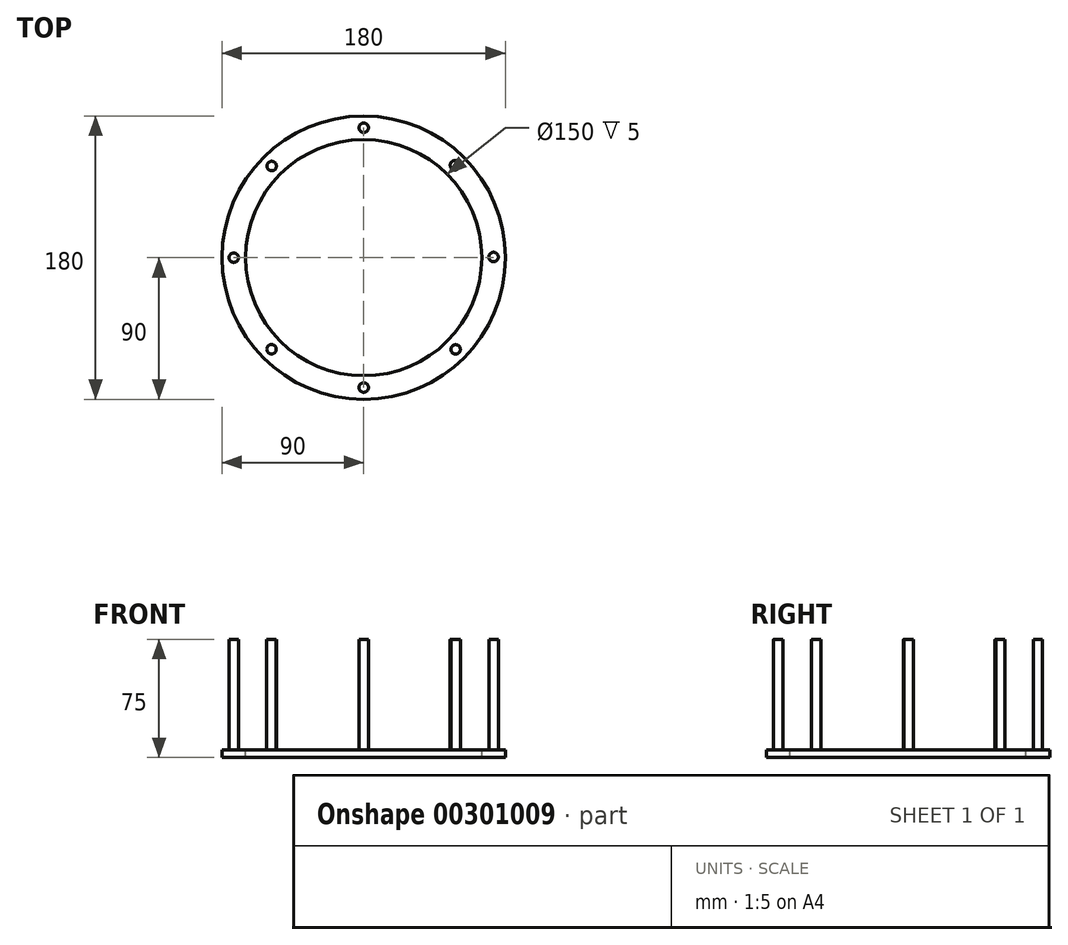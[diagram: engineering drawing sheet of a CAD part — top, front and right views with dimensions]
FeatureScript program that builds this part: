
annotation { "Feature Type Name" : "Feature", "Feature Type Description" : "" }
export const myFeature = defineFeature(function(context is Context, id is Id, definition is map)
    precondition{}
    {
        {
            var Q0;
            Q0=qCreatedBy(makeId("Top.planeOp"),FACE);
            var sketch = newSketch(context, id + "F0", { "sketchPlane" : qUnion([Q0])});
            skCircle(sketch, "E0", {"center": v(0, 0) * mm, "radius": 90 * mm});
            skCircle(sketch, "E1", {"center": v(0, 0) * mm, "radius": 75 * mm});
            skPoint(sketch, "E2", {"position": v(0, 82.48) * mm});
            skPoint(sketch, "E3", {"position": v(0, -82.5) * mm});
            skPoint(sketch, "E4", {"position": v(-75, 0) * mm});
            skPoint(sketch, "E5", {"position": v(-82.5, 0) * mm});
            skPoint(sketch, "E6", {"position": v(-58.44, 58.23) * mm});
            skPoint(sketch, "E7", {"position": v(82.5, 0.44) * mm});
            skPoint(sketch, "E8", {"position": v(57.94, 58.73) * mm});
            skPoint(sketch, "E9", {"position": v(-58.53, -58.15) * mm});
            skLineSegment(sketch, "E10", {"start": v(0, 0) * mm, "end": v(0, 0) * mm});
            skPoint(sketch, "E11", {"position": v(58.39, -58.28) * mm});
            skSolve(sketch);
        }
        {
            var Q0;
            Q0=makeQuery(id+"F0.imprint","IMPRINT",FACE,{"disambiguationData":[TD([[makeQuery(id+"F0.imprint","IMPRINT",EDGE,{"derivedFrom":sQuery(id+"F0.wireOp",EDGE,"E0")}),1.0]])]});
            extrude(context, id + "F1", {"entities" : qUnion([Q0]), "oppositeDirection" : true, "depth" : 5 * mm});
        }
        {
            var Q0;
            Q0=qCreatedBy(makeId("Top.planeOp"),FACE);
            var sketch = newSketch(context, id + "F2", { "sketchPlane" : qUnion([Q0])});
            skPoint(sketch, "E12", {"position": v(0, 82.5) * mm});
            skCircle(sketch, "E13", {"center": v(0, 82.5) * mm, "radius": 3 * mm});
            skCircle(sketch, "E14", {"center": v(57.94, 58.73) * mm, "radius": 3 * mm});
            skCircle(sketch, "E15", {"center": v(0, -82.5) * mm, "radius": 3 * mm});
            skCircle(sketch, "E16", {"center": v(-58.44, 58.22) * mm, "radius": 3 * mm});
            skCircle(sketch, "E17", {"center": v(-82.5, 0) * mm, "radius": 3 * mm});
            skCircle(sketch, "E18", {"center": v(58.4, -58.28) * mm, "radius": 3 * mm});
            skCircle(sketch, "E19", {"center": v(-58.53, -58.14) * mm, "radius": 3 * mm});
            skCircle(sketch, "E20", {"center": v(82.5, 0.44) * mm, "radius": 3 * mm});
            skSolve(sketch);
        }
        {
            var Q0;
            Q0=makeQuery(id+"F2.imprint","IMPRINT",FACE,{"disambiguationData":[TD([[makeQuery(id+"F2.imprint","IMPRINT",EDGE,{"derivedFrom":sQuery(id+"F2.wireOp",EDGE,"E13")}),1.0]])]});
            var Q1;
            Q1=makeQuery(id+"F2.imprint","IMPRINT",FACE,{"disambiguationData":[TD([[makeQuery(id+"F2.imprint","IMPRINT",EDGE,{"derivedFrom":sQuery(id+"F2.wireOp",EDGE,"E14")}),1.0]])]});
            var Q2;
            Q2=makeQuery(id+"F2.imprint","IMPRINT",FACE,{"disambiguationData":[TD([[makeQuery(id+"F2.imprint","IMPRINT",EDGE,{"derivedFrom":sQuery(id+"F2.wireOp",EDGE,"E20")}),1.0]])]});
            var Q3;
            Q3=makeQuery(id+"F2.imprint","IMPRINT",FACE,{"disambiguationData":[TD([[makeQuery(id+"F2.imprint","IMPRINT",EDGE,{"derivedFrom":sQuery(id+"F2.wireOp",EDGE,"E18")}),1.0]])]});
            var Q4;
            Q4=makeQuery(id+"F2.imprint","IMPRINT",FACE,{"disambiguationData":[TD([[makeQuery(id+"F2.imprint","IMPRINT",EDGE,{"derivedFrom":sQuery(id+"F2.wireOp",EDGE,"E15")}),1.0]])]});
            var Q5;
            Q5=makeQuery(id+"F2.imprint","IMPRINT",FACE,{"disambiguationData":[TD([[makeQuery(id+"F2.imprint","IMPRINT",EDGE,{"derivedFrom":sQuery(id+"F2.wireOp",EDGE,"E16")}),1.0]])]});
            var Q6;
            Q6=makeQuery(id+"F2.imprint","IMPRINT",FACE,{"disambiguationData":[TD([[makeQuery(id+"F2.imprint","IMPRINT",EDGE,{"derivedFrom":sQuery(id+"F2.wireOp",EDGE,"E17")}),1.0]])]});
            var Q7;
            Q7=makeQuery(id+"F2.imprint","IMPRINT",FACE,{"disambiguationData":[TD([[makeQuery(id+"F2.imprint","IMPRINT",EDGE,{"derivedFrom":sQuery(id+"F2.wireOp",EDGE,"E19")}),1.0]])]});
            extrude(context, id + "F3", {"entities" : qUnion([Q0, Q1, Q2, Q3, Q4, Q5, Q6, Q7]), "operationType" : NewBodyOperationType.ADD, "depth" : 70 * mm});
        }
    });
